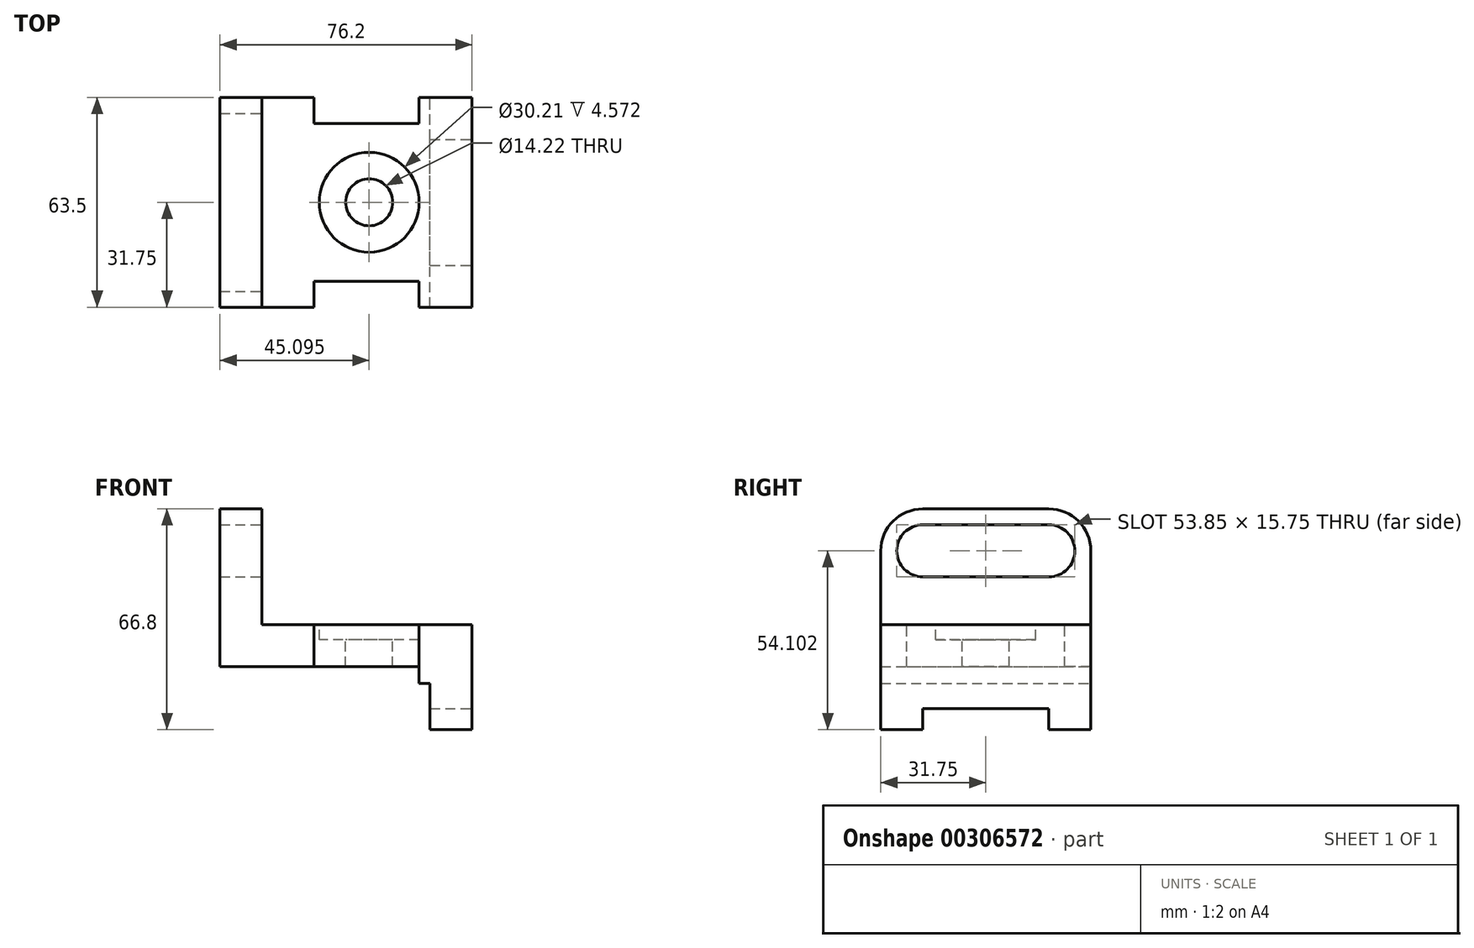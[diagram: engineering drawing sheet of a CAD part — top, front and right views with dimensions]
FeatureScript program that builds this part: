
annotation { "Feature Type Name" : "Feature", "Feature Type Description" : "" }
export const myFeature = defineFeature(function(context is Context, id is Id, definition is map)
    precondition{}
    {
        {
            var Q0;
            Q0=qCreatedBy(makeId("Front.planeOp"),FACE);
            var sketch = newSketch(context, id + "F0", { "sketchPlane" : qUnion([Q0])});
            skLineSegment(sketch, "E0", {"start": v(0, 0) * mm, "end": v(0, 47.75) * mm});
            skLineSegment(sketch, "E1", {"start": v(0, 47.75) * mm, "end": v(12.7, 47.75) * mm});
            skLineSegment(sketch, "E2", {"start": v(12.7, 47.75) * mm, "end": v(12.7, 12.7) * mm});
            skLineSegment(sketch, "E3", {"start": v(12.7, 12.7) * mm, "end": v(76.2, 12.7) * mm});
            skLineSegment(sketch, "E4", {"start": v(76.2, 12.7) * mm, "end": v(76.2, -19.05) * mm});
            skLineSegment(sketch, "E5", {"start": v(76.2, -19.05) * mm, "end": v(63.5, -19.05) * mm});
            skLineSegment(sketch, "E6", {"start": v(0, 0) * mm, "end": v(60.2, 0) * mm});
            skLineSegment(sketch, "E7", {"start": v(60.2, 0) * mm, "end": v(60.2, -5.08) * mm});
            skLineSegment(sketch, "E8", {"start": v(60.2, -5.08) * mm, "end": v(63.5, -5.08) * mm});
            skLineSegment(sketch, "E9", {"start": v(63.5, -5.08) * mm, "end": v(63.5, -19.05) * mm});
            skSolve(sketch);
        }
        {
            var Q0;
            Q0 = qSketchRegion(id + "F0", true);
            extrude(context, id + "F1", {"entities" : qUnion([Q0]), "depth" : 63.5 * mm});
        }
        {
            var Q0;
            Q0=makeQuery(id+"F1.opExtrude","CAP_EDGE",EDGE,{"disambiguationData":[OSD([sQuery(id+"F0.wireOp",EDGE,"E1")])],"isStart":false});
            var Q1;
            Q1=makeQuery(id+"F1.opExtrude","CAP_EDGE",EDGE,{"disambiguationData":[OSD([sQuery(id+"F0.wireOp",EDGE,"E1")])],"isStart":true});
            fillet(context, id + "F2", {"entities" : qUnion([Q0, Q1]), "radius" : 12.7 * mm, "tangentPropagation" : true, "allowEdgeOverflow" : false});
        }
        {
            var Q0;
            Q0=makeQuery(id+"F1.opExtrude","SWEPT_FACE",FACE,{"disambiguationData":[OSD([sQuery(id+"F0.wireOp",EDGE,"E4")])]});
            var sketch = newSketch(context, id + "F3", { "sketchPlane" : qUnion([Q0])});
            skLineSegment(sketch, "E10", {"start": v(-50.8, -19.05) * mm, "end": v(-50.8, -12.7) * mm});
            skLineSegment(sketch, "E11", {"start": v(-50.8, -12.7) * mm, "end": v(-12.7, -12.7) * mm});
            skLineSegment(sketch, "E12", {"start": v(-12.7, -12.7) * mm, "end": v(-12.7, -19.05) * mm});
            skLineSegment(sketch, "E13", {"start": v(-12.7, -19.05) * mm, "end": v(-50.8, -19.05) * mm});
            skSolve(sketch);
        }
        {
            var Q0;
            Q0 = qSketchRegion(id + "F3", true);
            extrude(context, id + "F4", {"entities" : qUnion([Q0]), "operationType" : NewBodyOperationType.REMOVE, "oppositeDirection" : true, "depth" : 25.4 * mm});
        }
        {
            var Q0;
            Q0=makeQuery(id+"F1.opExtrude","SWEPT_FACE",FACE,{"disambiguationData":[OSD([sQuery(id+"F0.wireOp",EDGE,"E3")])]});
            var sketch = newSketch(context, id + "F5", { "sketchPlane" : qUnion([Q0])});
            skLineSegment(sketch, "E14", {"start": v(28.45, -63.5) * mm, "end": v(28.45, -55.63) * mm});
            skLineSegment(sketch, "E15", {"start": v(28.45, -55.63) * mm, "end": v(60.2, -55.63) * mm});
            skLineSegment(sketch, "E16", {"start": v(60.2, -55.63) * mm, "end": v(60.2, -63.5) * mm});
            skLineSegment(sketch, "E17", {"start": v(60.2, -63.5) * mm, "end": v(28.45, -63.5) * mm});
            skLineSegment(sketch, "E18", {"start": v(28.45, 0) * mm, "end": v(28.45, -7.87) * mm});
            skLineSegment(sketch, "E19", {"start": v(28.45, -7.87) * mm, "end": v(60.2, -7.87) * mm});
            skLineSegment(sketch, "E20", {"start": v(60.2, -7.87) * mm, "end": v(60.2, 0) * mm});
            skLineSegment(sketch, "E21", {"start": v(60.2, 0) * mm, "end": v(28.45, 0) * mm});
            skSolve(sketch);
        }
        {
            var Q0;
            Q0 = qSketchRegion(id + "F5", true);
            extrude(context, id + "F6", {"entities" : qUnion([Q0]), "operationType" : NewBodyOperationType.REMOVE, "oppositeDirection" : true, "depth" : 25.4 * mm});
        }
        {
            var Q0;
            Q0=makeQuery(id+"F1.opExtrude","SWEPT_FACE",FACE,{"disambiguationData":[OSD([sQuery(id+"F0.wireOp",EDGE,"E2")])]});
            var sketch = newSketch(context, id + "F7", { "sketchPlane" : qUnion([Q0])});
            skLineSegment(sketch, "E22", {"start": v(-50.8, 42.93) * mm, "end": v(-12.7, 42.93) * mm});
            skLineSegment(sketch, "E23", {"start": v(-50.8, 27.18) * mm, "end": v(-12.7, 27.18) * mm});
            skArc(sketch, "E24", {"start": v(-50.8, 42.93) * mm, "mid": v(-58.67, 35.05) * mm, "end": v(-50.8, 27.18) * mm});
            skArc(sketch, "E25", {"start": v(-12.7, 42.93) * mm, "mid": v(-4.83, 35.05) * mm, "end": v(-12.7, 27.18) * mm});
            skSolve(sketch);
        }
        {
            var Q0;
            Q0=makeQuery(id+"F1.opExtrude","SWEPT_FACE",FACE,{"disambiguationData":[OSD([sQuery(id+"F0.wireOp",EDGE,"E3")])]});
            var sketch = newSketch(context, id + "F8", { "sketchPlane" : qUnion([Q0])});
            skCircle(sketch, "E26", {"center": v(45.1, -31.75) * mm, "radius": 15.1 * mm});
            skSolve(sketch);
        }
        {
            var Q0;
            Q0 = qSketchRegion(id + "F8", true);
            extrude(context, id + "F9", {"entities" : qUnion([Q0]), "operationType" : NewBodyOperationType.REMOVE, "oppositeDirection" : true, "depth" : 4.57 * mm});
        }
        {
            var Q0;
            Q0=makeQuery(id+"F9.boolean.opBoolean","COPY",FACE,{"derivedFrom":makeQuery(id+"F9.opExtrude","CAP_FACE",FACE,{"disambiguationData":[OSD([sQuery(id+"F8.wireOp",EDGE,"E26")])],"isStart":false})});
            var sketch = newSketch(context, id + "F10", { "sketchPlane" : qUnion([Q0])});
            skCircle(sketch, "E27", {"center": v(45.1, -31.75) * mm, "radius": 7.11 * mm});
            skSolve(sketch);
        }
        {
            var Q0;
            Q0 = qSketchRegion(id + "F10", true);
            extrude(context, id + "F11", {"entities" : qUnion([Q0]), "operationType" : NewBodyOperationType.REMOVE, "endBound" : BoundingType.THROUGH_ALL, "oppositeDirection" : true, "depth" : 25.4 * mm});
        }
        {
            var Q0;
            Q0 = qSketchRegion(id + "F7", true);
            extrude(context, id + "F12", {"entities" : qUnion([Q0]), "operationType" : NewBodyOperationType.REMOVE, "oppositeDirection" : true, "depth" : 25.4 * mm});
        }
        {
            var Q0;
            Q0 = qSketchRegion(id + "F7", true);
            extrude(context, id + "F13", {"entities" : qUnion([Q0]), "operationType" : NewBodyOperationType.REMOVE, "endBound" : BoundingType.THROUGH_ALL, "oppositeDirection" : true, "depth" : 25.4 * mm});
        }
    });
